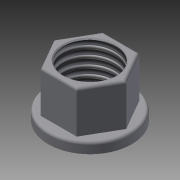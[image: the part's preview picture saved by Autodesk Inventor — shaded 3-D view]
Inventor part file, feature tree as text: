
AUTODESK INVENTOR PART (.ipt)
format: ipt  version: 2015 (Build 190159000, 159)  size: 129,024 bytes
history: native  units: mm
features: extrude x3, sketch x3, thread x1, fillet x1, chamfer x1
ambient origin geometry x8: Origin, YZ Plane, XZ Plane, XY Plane, X Axis, Y Axis, Z Axis, Center Point
bodies: 实体1 (feature_tree)
feature tree (9):
  extrude  "拉伸1"  Depth=1.0mm TaperAngle=0.0deg
  extrude  "拉伸2"  Depth=6.0mm
  extrude  "拉伸3"  Depth=5.0mm
  thread  "螺纹1"  [1 undecoded]
  fillet  "圆角1"  Radius=10.0mm
  chamfer  "倒角1"  Distance=0.25mm
  sketch  "草图1"  dims[d0=8.0mm d1=1.0mm d2=0.0mm]
  sketch  "草图2"  dims[d3=0.964441mm d4=6.0mm]
  sketch  "草图3"  dims[d5=4.0mm d6=0.0mm d7=5.0mm d8=4.0mm d9=0.0mm d10=10.0mm d11=0.0mm d12=0.25mm d13=0.1mm d14=2.0mm d15=45.0deg]
note: 1 required parameter value undecoded (feature->parameter linkage not recoverable at this tier; creation-order binding heuristic only, values carry confidence <= 0.55)
